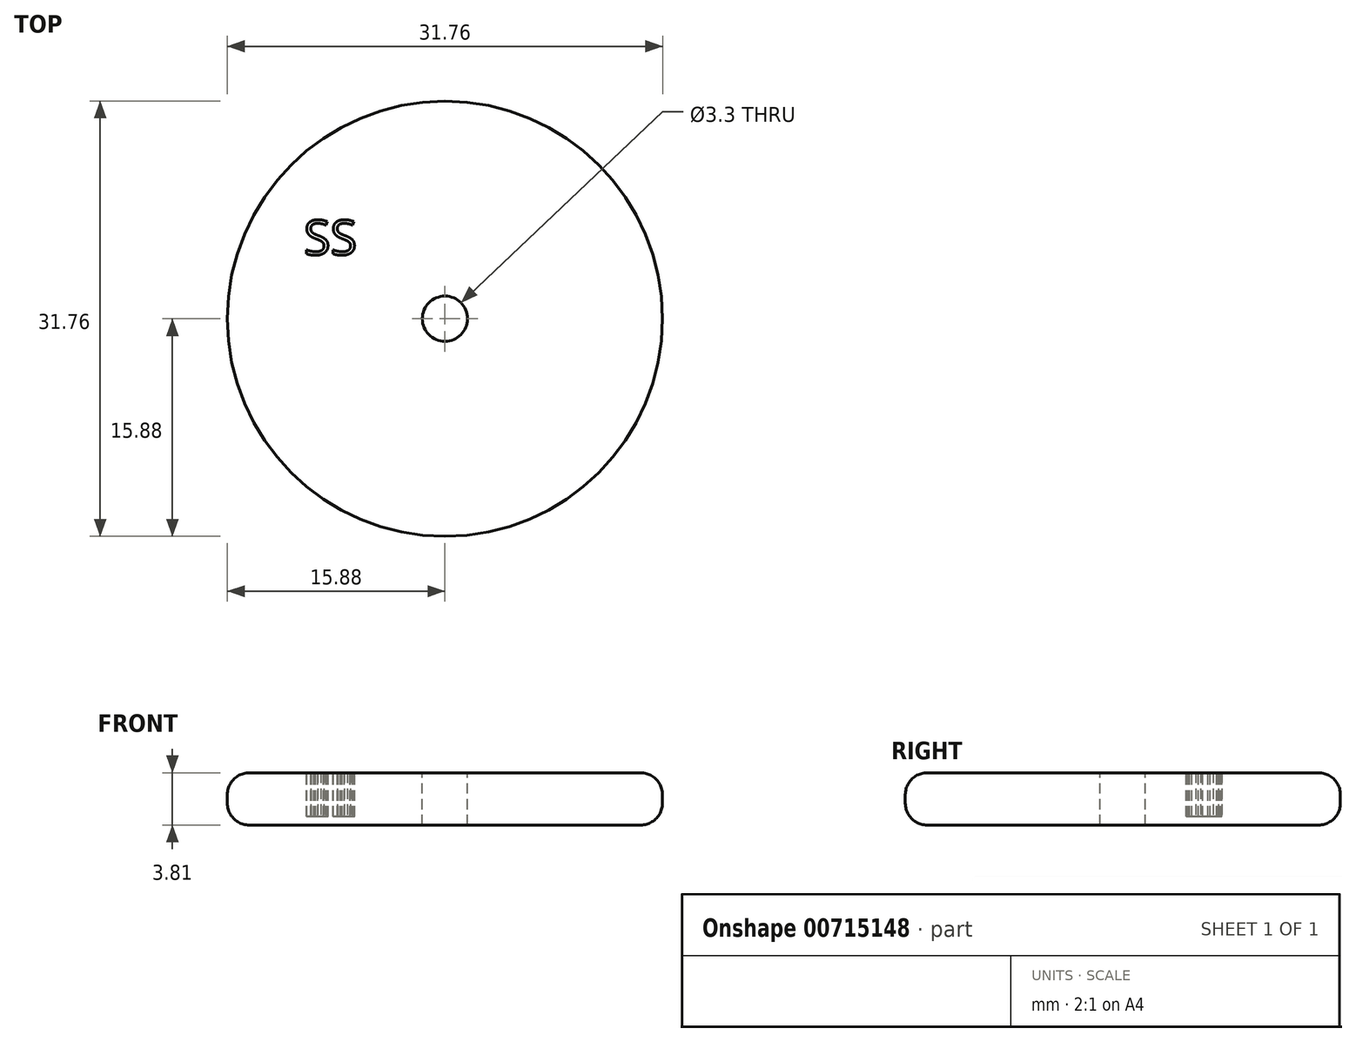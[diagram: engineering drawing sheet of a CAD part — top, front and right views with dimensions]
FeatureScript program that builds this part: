
annotation { "Feature Type Name" : "Feature", "Feature Type Description" : "" }
export const myFeature = defineFeature(function(context is Context, id is Id, definition is map)
    precondition{}
    {
        {
            var Q0;
            Q0=qCreatedBy(makeId("Top.planeOp"),FACE);
            var sketch = newSketch(context, id + "F0", { "sketchPlane" : qUnion([Q0])});
            skCircle(sketch, "E0", {"center": v(0, 0) * mm, "radius": 15.88 * mm});
            skSolve(sketch);
        }
        {
            var Q0;
            Q0 = qSketchRegion(id + "F0", true);
            extrude(context, id + "F1", {"entities" : qUnion([Q0]), "depth" : 3.8 * mm, "offsetDistance" : 25.4 * mm});
        }
        {
            var Q0;
            Q0=makeQuery(id+"F1.opExtrude","CAP_FACE",FACE,{"disambiguationData":[OSD([sQuery(id+"F0.wireOp",EDGE,"E0")])],"isStart":false});
            var sketch = newSketch(context, id + "F2", { "sketchPlane" : qUnion([Q0])});
            skCircle(sketch, "E1", {"center": v(0, 0) * mm, "radius": 1.65 * mm});
            skSolve(sketch);
        }
        {
            var Q0;
            Q0 = qSketchRegion(id + "F2", true);
            extrude(context, id + "F3", {"entities" : qUnion([Q0]), "operationType" : NewBodyOperationType.REMOVE, "endBound" : BoundingType.THROUGH_ALL, "oppositeDirection" : true, "depth" : 25.4 * mm, "offsetDistance" : 25.4 * mm});
        }
        {
            var Q0;
            Q0=makeQuery(id+"F1.opExtrude","CAP_EDGE",EDGE,{"disambiguationData":[OSD([sQuery(id+"F0.wireOp",EDGE,"E0")])],"isStart":false});
            var Q1;
            Q1=makeQuery(id+"F1.opExtrude","CAP_EDGE",EDGE,{"disambiguationData":[OSD([sQuery(id+"F0.wireOp",EDGE,"E0")])],"isStart":true});
            fillet(context, id + "F4", {"entities" : qUnion([Q0, Q1]), "radius" : 1.59 * mm, "tangentPropagation" : true, "allowEdgeOverflow" : false});
        }
        {
            var Q0;
            Q0=makeQuery(id+"F1.opExtrude","CAP_FACE",FACE,{"disambiguationData":[OSD([sQuery(id+"F0.wireOp",EDGE,"E0")])],"isStart":false});
            var sketch = newSketch(context, id + "F5", { "sketchPlane" : qUnion([Q0])});
            skText(sketch, "E2", { "text": "SS\n", "fontName": "OpenSans-Regular.ttf"});
            const initialGuessF5  = {"E2": [-0.0103, 0.00467, 1, 0, 0.00254]};
            skSetInitialGuess(sketch, initialGuessF5);
            skSolve(sketch);
        }
        {
            var Q0;
            Q0 = qSketchRegion(id + "F5", true);
            extrude(context, id + "F6", {"entities" : qUnion([Q0]), "operationType" : NewBodyOperationType.REMOVE, "oppositeDirection" : true, "depth" : 3.17 * mm, "offsetDistance" : 25.4 * mm});
        }
    });
